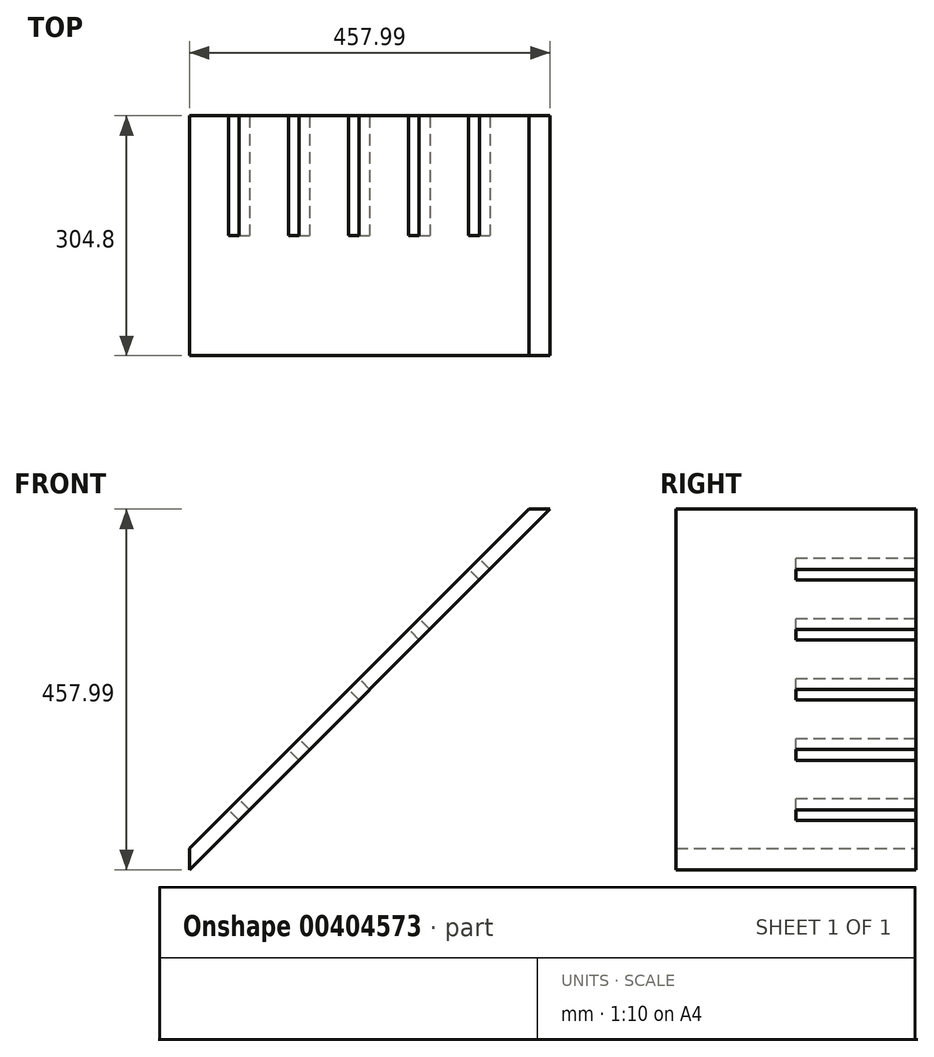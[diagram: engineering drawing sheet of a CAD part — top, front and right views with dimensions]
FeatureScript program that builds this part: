
annotation { "Feature Type Name" : "Feature", "Feature Type Description" : "" }
export const myFeature = defineFeature(function(context is Context, id is Id, definition is map)
    precondition{}
    {
        {
            var Q0;
            Q0=qCreatedBy(makeId("Front.planeOp"),FACE);
            var sketch = newSketch(context, id + "F0", { "sketchPlane" : qUnion([Q0])});
            skLineSegment(sketch, "E0.left", {"start": v(-421.52, 0) * mm, "end": v(-421.52, 26.94) * mm});
            skPoint(sketch, "E0.middle", {"position": v(22.97, 488.94) * mm});
            skLineSegment(sketch, "E1", {"start": v(-421.52, 0) * mm, "end": v(36.47, 458) * mm});
            skLineSegment(sketch, "E2", {"start": v(-421.52, 26.94) * mm, "end": v(9.53, 458) * mm});
            skLineSegment(sketch, "E3", {"start": v(36.47, 458) * mm, "end": v(9.53, 458) * mm});
            skSolve(sketch);
        }
        {
            var Q0;
            Q0=qSketchRegion(id+"F0",true);
            extrude(context, id + "F1", {"entities" : qUnion([Q0]), "endBound" : BoundingType.SYMMETRIC, "depth" : 304.8 * mm});
        }
        {
            var Q0;
            Q0=makeQuery(id+"F1.opExtrude","SWEPT_FACE",FACE,{"disambiguationData":[OSD([sQuery(id+"F0.wireOp",EDGE,"E2")])]});
            var sketch = newSketch(context, id + "F2", { "sketchPlane" : qUnion([Q0])});
            skLineSegment(sketch, "E4.bottom", {"start": v(-152.4, -209.16) * mm, "end": v(0, -209.16) * mm});
            skLineSegment(sketch, "E4.top", {"start": v(-152.4, -190.11) * mm, "end": v(0, -190.11) * mm});
            skLineSegment(sketch, "E4.left", {"start": v(-152.4, -209.16) * mm, "end": v(-152.4, -190.11) * mm});
            skLineSegment(sketch, "E4.right", {"start": v(0, -209.16) * mm, "end": v(0, -190.11) * mm});
            skLineSegment(sketch, "E5.bottom", {"start": v(-152.4, -101.21) * mm, "end": v(0, -101.21) * mm});
            skLineSegment(sketch, "E5.top", {"start": v(-152.4, -82.16) * mm, "end": v(0, -82.16) * mm});
            skLineSegment(sketch, "E5.left", {"start": v(-152.4, -101.21) * mm, "end": v(-152.4, -82.16) * mm});
            skLineSegment(sketch, "E5.right", {"start": v(0, -101.21) * mm, "end": v(0, -82.16) * mm});
            skLineSegment(sketch, "E6.bottom", {"start": v(-152.4, 6.74) * mm, "end": v(0, 6.74) * mm});
            skLineSegment(sketch, "E6.top", {"start": v(-152.4, 25.79) * mm, "end": v(0, 25.79) * mm});
            skLineSegment(sketch, "E6.left", {"start": v(-152.4, 6.74) * mm, "end": v(-152.4, 25.79) * mm});
            skLineSegment(sketch, "E6.right", {"start": v(0, 6.74) * mm, "end": v(0, 25.79) * mm});
            skLineSegment(sketch, "E7.bottom", {"start": v(-152.4, 114.69) * mm, "end": v(0, 114.69) * mm});
            skLineSegment(sketch, "E7.top", {"start": v(-152.4, 133.74) * mm, "end": v(0, 133.74) * mm});
            skLineSegment(sketch, "E7.left", {"start": v(-152.4, 114.69) * mm, "end": v(-152.4, 133.74) * mm});
            skLineSegment(sketch, "E7.right", {"start": v(0, 114.69) * mm, "end": v(0, 133.74) * mm});
            skLineSegment(sketch, "E8.bottom", {"start": v(-152.4, 222.64) * mm, "end": v(0, 222.64) * mm});
            skLineSegment(sketch, "E8.top", {"start": v(-152.4, 241.69) * mm, "end": v(0, 241.69) * mm});
            skLineSegment(sketch, "E8.left", {"start": v(-152.4, 222.64) * mm, "end": v(-152.4, 241.69) * mm});
            skLineSegment(sketch, "E8.right", {"start": v(0, 222.64) * mm, "end": v(0, 241.69) * mm});
            skSolve(sketch);
        }
        {
            var Q0;
            Q0=qSketchRegion(id+"F2",true);
            extrude(context, id + "F3", {"entities" : qUnion([Q0]), "operationType" : NewBodyOperationType.REMOVE, "oppositeDirection" : true, "depth" : 19.05 * mm});
        }
    });
